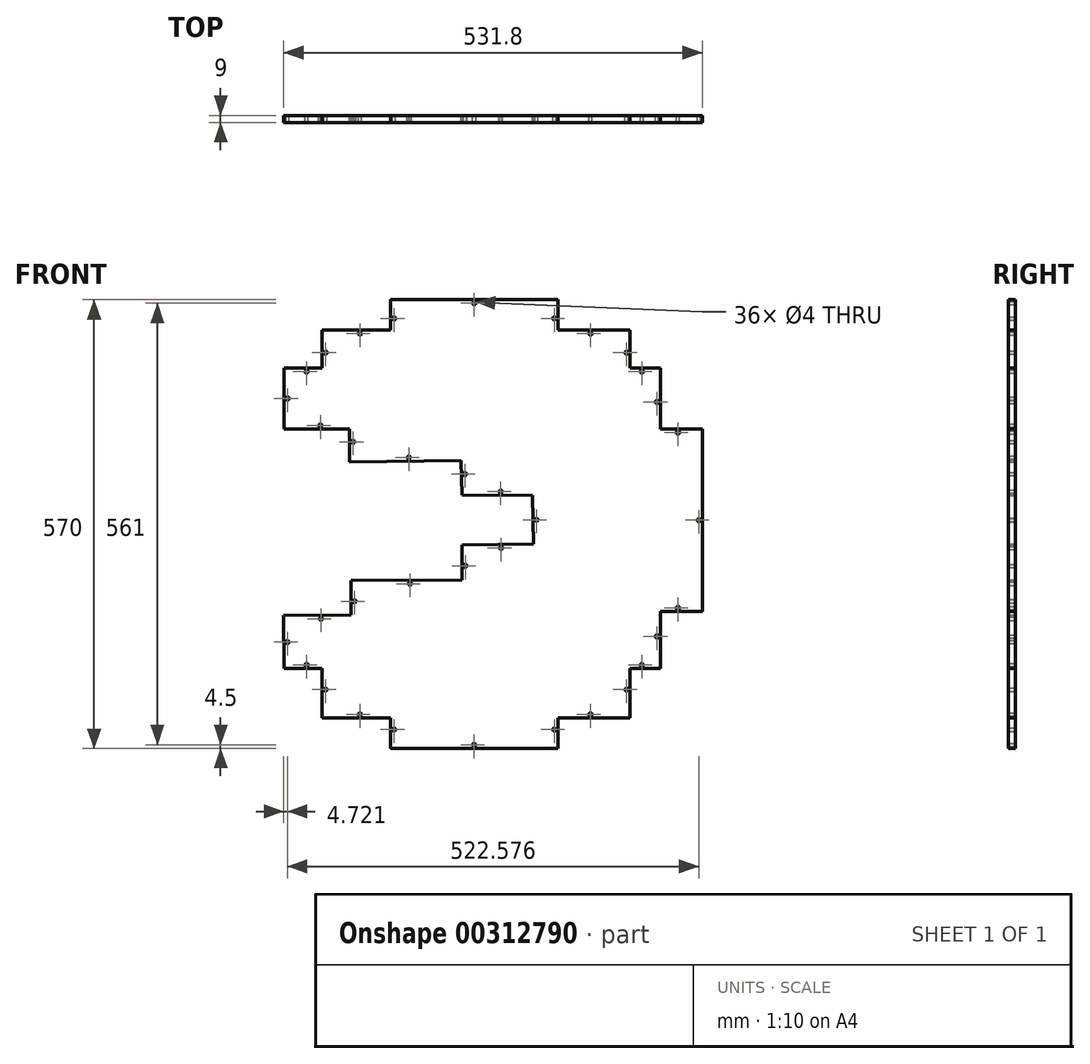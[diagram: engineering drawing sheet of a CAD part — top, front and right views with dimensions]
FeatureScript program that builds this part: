
annotation { "Feature Type Name" : "Feature", "Feature Type Description" : "" }
export const myFeature = defineFeature(function(context is Context, id is Id, definition is map)
    precondition{}
    {
        {
            var Q0;
            Q0=qCreatedBy(makeId("Front.planeOp"),FACE);
            var sketch = newSketch(context, id + "F0", { "sketchPlane" : qUnion([Q0])});
            skLineSegment(sketch, "E0", {"start": v(265.9, 120.76) * mm, "end": v(212.76, 120.76) * mm});
            skLineSegment(sketch, "E1", {"start": v(212.76, 120.76) * mm, "end": v(212.76, 198.05) * mm});
            skLineSegment(sketch, "E2", {"start": v(212.76, 198.05) * mm, "end": v(174.11, 198.05) * mm});
            skLineSegment(sketch, "E3", {"start": v(174.11, 198.05) * mm, "end": v(174.11, 246.35) * mm});
            skLineSegment(sketch, "E4", {"start": v(174.11, 246.35) * mm, "end": v(82.34, 246.35) * mm});
            skLineSegment(sketch, "E5", {"start": v(82.34, 246.35) * mm, "end": v(82.34, 285) * mm});
            skLineSegment(sketch, "E6", {"start": v(82.34, 285) * mm, "end": v(-130.2, 285) * mm});
            skLineSegment(sketch, "E7", {"start": v(-130.2, 285) * mm, "end": v(-130.2, 246.35) * mm});
            skLineSegment(sketch, "E8", {"start": v(-130.2, 246.35) * mm, "end": v(-217.15, 246.35) * mm});
            skLineSegment(sketch, "E9", {"start": v(-217.15, 246.35) * mm, "end": v(-217.15, 198.05) * mm});
            skLineSegment(sketch, "E10", {"start": v(-217.15, 198.05) * mm, "end": v(-265.46, 198.05) * mm});
            skLineSegment(sketch, "E11", {"start": v(-265.46, 198.05) * mm, "end": v(-265.46, 120.76) * mm});
            skLineSegment(sketch, "E12", {"start": v(-265.46, 120.76) * mm, "end": v(-182.22, 120.66) * mm});
            skLineSegment(sketch, "E13", {"start": v(-182.22, 120.66) * mm, "end": v(-182.3, 79) * mm});
            skLineSegment(sketch, "E14", {"start": v(-182.3, 79) * mm, "end": v(-40.62, 80.76) * mm});
            skLineSegment(sketch, "E15", {"start": v(-40.62, 80.76) * mm, "end": v(-39.72, 37.15) * mm});
            skLineSegment(sketch, "E16", {"start": v(-39.72, 37.15) * mm, "end": v(50.2, 36.25) * mm});
            skLineSegment(sketch, "E17", {"start": v(50.2, 36.25) * mm, "end": v(51.12, -25.52) * mm});
            skLineSegment(sketch, "E18", {"start": v(51.12, -25.52) * mm, "end": v(-39.72, -26.43) * mm});
            skLineSegment(sketch, "E19", {"start": v(-39.72, -26.43) * mm, "end": v(-39.72, -70.94) * mm});
            skLineSegment(sketch, "E20", {"start": v(-39.72, -70.94) * mm, "end": v(-180.51, -71.85) * mm});
            skLineSegment(sketch, "E21", {"start": v(-180.51, -71.85) * mm, "end": v(-180.51, -115.45) * mm});
            skLineSegment(sketch, "E22", {"start": v(-180.51, -115.45) * mm, "end": v(-265.9, -116.36) * mm});
            skLineSegment(sketch, "E23", {"start": v(-265.9, -116.36) * mm, "end": v(-265.46, -183.56) * mm});
            skLineSegment(sketch, "E24", {"start": v(-265.46, -183.56) * mm, "end": v(-217.15, -183.56) * mm});
            skLineSegment(sketch, "E25", {"start": v(-217.15, -183.56) * mm, "end": v(-217.15, -246.36) * mm});
            skLineSegment(sketch, "E26", {"start": v(-217.15, -246.36) * mm, "end": v(-130.2, -246.36) * mm});
            skLineSegment(sketch, "E27", {"start": v(-130.2, -246.36) * mm, "end": v(-130.2, -285) * mm});
            skLineSegment(sketch, "E28", {"start": v(-130.2, -285) * mm, "end": v(82.34, -285) * mm});
            skLineSegment(sketch, "E29", {"start": v(82.34, -285) * mm, "end": v(82.34, -246.36) * mm});
            skLineSegment(sketch, "E30", {"start": v(82.34, -246.36) * mm, "end": v(174.11, -246.36) * mm});
            skLineSegment(sketch, "E31", {"start": v(174.11, -246.36) * mm, "end": v(174.11, -183.56) * mm});
            skLineSegment(sketch, "E32", {"start": v(174.11, -183.56) * mm, "end": v(212.76, -183.56) * mm});
            skLineSegment(sketch, "E33", {"start": v(212.76, -183.56) * mm, "end": v(212.76, -111.1) * mm});
            skLineSegment(sketch, "E34", {"start": v(212.76, -111.1) * mm, "end": v(265.9, -111.1) * mm});
            skLineSegment(sketch, "E35", {"start": v(265.9, -111.1) * mm, "end": v(265.9, 120.76) * mm});
            skLineSegment(sketch, "E36.0", {"start": v(261.4, 116.26) * mm, "end": v(208.26, 116.26) * mm, "construction": true});
            skLineSegment(sketch, "E36.1", {"start": v(261.4, -106.6) * mm, "end": v(261.4, 116.26) * mm, "construction": true});
            skLineSegment(sketch, "E36.2", {"start": v(208.26, -106.6) * mm, "end": v(261.4, -106.6) * mm, "construction": true});
            skLineSegment(sketch, "E36.3", {"start": v(208.26, -179.06) * mm, "end": v(208.26, -106.6) * mm, "construction": true});
            skLineSegment(sketch, "E36.4", {"start": v(169.61, -179.06) * mm, "end": v(208.26, -179.06) * mm, "construction": true});
            skLineSegment(sketch, "E36.5", {"start": v(169.61, -241.86) * mm, "end": v(169.61, -179.06) * mm, "construction": true});
            skLineSegment(sketch, "E36.6", {"start": v(77.84, -241.86) * mm, "end": v(169.61, -241.86) * mm, "construction": true});
            skLineSegment(sketch, "E36.7", {"start": v(77.84, -280.5) * mm, "end": v(77.84, -241.86) * mm, "construction": true});
            skLineSegment(sketch, "E36.8", {"start": v(-125.7, -280.5) * mm, "end": v(77.84, -280.5) * mm, "construction": true});
            skLineSegment(sketch, "E36.9", {"start": v(-125.7, -241.86) * mm, "end": v(-125.7, -280.5) * mm, "construction": true});
            skLineSegment(sketch, "E36.10", {"start": v(-212.65, -241.86) * mm, "end": v(-125.7, -241.86) * mm, "construction": true});
            skLineSegment(sketch, "E36.11", {"start": v(208.26, 116.26) * mm, "end": v(208.26, 193.55) * mm, "construction": true});
            skLineSegment(sketch, "E36.12", {"start": v(-212.65, -179.06) * mm, "end": v(-212.65, -241.86) * mm, "construction": true});
            skLineSegment(sketch, "E36.13", {"start": v(-261, -179.06) * mm, "end": v(-212.65, -179.06) * mm, "construction": true});
            skLineSegment(sketch, "E36.14", {"start": v(-260.96, 193.55) * mm, "end": v(-260.96, 125.26) * mm, "construction": true});
            skLineSegment(sketch, "E36.15", {"start": v(-212.65, 193.55) * mm, "end": v(-260.96, 193.55) * mm, "construction": true});
            skLineSegment(sketch, "E36.16", {"start": v(-212.65, 241.85) * mm, "end": v(-212.65, 193.55) * mm, "construction": true});
            skLineSegment(sketch, "E36.17", {"start": v(-125.7, 241.85) * mm, "end": v(-212.65, 241.85) * mm, "construction": true});
            skLineSegment(sketch, "E36.18", {"start": v(-125.7, 280.5) * mm, "end": v(-125.7, 241.85) * mm, "construction": true});
            skLineSegment(sketch, "E36.19", {"start": v(77.84, 280.5) * mm, "end": v(-125.7, 280.5) * mm, "construction": true});
            skLineSegment(sketch, "E36.20", {"start": v(208.26, 193.55) * mm, "end": v(169.61, 193.55) * mm, "construction": true});
            skLineSegment(sketch, "E36.21", {"start": v(169.61, 193.55) * mm, "end": v(169.61, 241.85) * mm, "construction": true});
            skLineSegment(sketch, "E36.22", {"start": v(169.61, 241.85) * mm, "end": v(77.84, 241.85) * mm, "construction": true});
            skLineSegment(sketch, "E36.23", {"start": v(77.84, 241.85) * mm, "end": v(77.84, 280.5) * mm, "construction": true});
            skLineSegment(sketch, "E36.24", {"start": v(-260.96, 125.26) * mm, "end": v(-177.7, 125.15) * mm, "construction": true});
            skLineSegment(sketch, "E36.25", {"start": v(-177.7, 125.15) * mm, "end": v(-177.78, 83.55) * mm, "construction": true});
            skLineSegment(sketch, "E36.26", {"start": v(-177.78, 83.55) * mm, "end": v(-36.22, 85.31) * mm, "construction": true});
            skLineSegment(sketch, "E36.27", {"start": v(-36.22, 85.31) * mm, "end": v(-35.3, 41.6) * mm, "construction": true});
            skLineSegment(sketch, "E36.28", {"start": v(-35.3, 41.6) * mm, "end": v(54.64, 40.7) * mm, "construction": true});
            skLineSegment(sketch, "E36.29", {"start": v(54.64, 40.7) * mm, "end": v(55.69, -29.97) * mm, "construction": true});
            skLineSegment(sketch, "E36.30", {"start": v(55.69, -29.97) * mm, "end": v(-35.22, -30.88) * mm, "construction": true});
            skLineSegment(sketch, "E36.31", {"start": v(-35.22, -30.88) * mm, "end": v(-35.22, -75.4) * mm, "construction": true});
            skLineSegment(sketch, "E36.32", {"start": v(-35.22, -75.4) * mm, "end": v(-176.01, -76.32) * mm, "construction": true});
            skLineSegment(sketch, "E36.33", {"start": v(-176.01, -76.32) * mm, "end": v(-176.01, -119.9) * mm, "construction": true});
            skLineSegment(sketch, "E36.34", {"start": v(-176.01, -119.9) * mm, "end": v(-261.37, -120.82) * mm, "construction": true});
            skLineSegment(sketch, "E36.35", {"start": v(-261.37, -120.82) * mm, "end": v(-261, -179.06) * mm, "construction": true});
            skCircle(sketch, "E37", {"center": v(-23.93, 280.5) * mm, "radius": 2 * mm});
            skCircle(sketch, "E38", {"center": v(-125.7, 261.18) * mm, "radius": 2 * mm});
            skCircle(sketch, "E39", {"center": v(-169.17, 241.85) * mm, "radius": 2 * mm});
            skCircle(sketch, "E40", {"center": v(-212.65, 217.7) * mm, "radius": 2 * mm});
            skCircle(sketch, "E41", {"center": v(-236.8, 193.55) * mm, "radius": 2 * mm});
            skCircle(sketch, "E42", {"center": v(-260.96, 159.4) * mm, "radius": 2 * mm});
            skCircle(sketch, "E43", {"center": v(-219.33, 125.2) * mm, "radius": 2 * mm});
            skCircle(sketch, "E44", {"center": v(-177.75, 104.35) * mm, "radius": 2 * mm});
            skCircle(sketch, "E45", {"center": v(-107, 84.43) * mm, "radius": 2 * mm});
            skCircle(sketch, "E46", {"center": v(-35.76, 63.46) * mm, "radius": 2 * mm});
            skCircle(sketch, "E47", {"center": v(9.67, 41.16) * mm, "radius": 2 * mm});
            skCircle(sketch, "E48", {"center": v(77.84, 261.18) * mm, "radius": 2 * mm});
            skCircle(sketch, "E49", {"center": v(123.73, 241.85) * mm, "radius": 2 * mm});
            skCircle(sketch, "E50", {"center": v(169.61, 217.7) * mm, "radius": 2 * mm});
            skCircle(sketch, "E51", {"center": v(188.94, 193.55) * mm, "radius": 2 * mm});
            skCircle(sketch, "E52", {"center": v(208.26, 154.9) * mm, "radius": 2 * mm});
            skCircle(sketch, "E53", {"center": v(234.83, 116.26) * mm, "radius": 2 * mm});
            skCircle(sketch, "E54", {"center": v(261.4, 4.83) * mm, "radius": 2 * mm});
            skCircle(sketch, "E55", {"center": v(234.83, -106.6) * mm, "radius": 2 * mm});
            skCircle(sketch, "E56", {"center": v(55.17, 5.36) * mm, "radius": 2 * mm});
            skCircle(sketch, "E57", {"center": v(10.24, -30.43) * mm, "radius": 2 * mm});
            skCircle(sketch, "E58", {"center": v(-35.22, -53.15) * mm, "radius": 2 * mm});
            skCircle(sketch, "E59", {"center": v(-105.61, -75.86) * mm, "radius": 2 * mm});
            skCircle(sketch, "E60", {"center": v(-176.01, -98.1) * mm, "radius": 2 * mm});
            skCircle(sketch, "E61", {"center": v(-218.69, -120.36) * mm, "radius": 2 * mm});
            skCircle(sketch, "E62", {"center": v(-261.18, -149.94) * mm, "radius": 2 * mm});
            skCircle(sketch, "E63", {"center": v(-236.82, -179.06) * mm, "radius": 2 * mm});
            skCircle(sketch, "E64", {"center": v(-212.65, -210.46) * mm, "radius": 2 * mm});
            skCircle(sketch, "E65", {"center": v(-169.17, -241.86) * mm, "radius": 2 * mm});
            skCircle(sketch, "E66", {"center": v(-125.7, -261.18) * mm, "radius": 2 * mm});
            skCircle(sketch, "E67", {"center": v(-23.93, -280.5) * mm, "radius": 2 * mm});
            skCircle(sketch, "E68", {"center": v(77.84, -261.18) * mm, "radius": 2 * mm});
            skCircle(sketch, "E69", {"center": v(123.73, -241.86) * mm, "radius": 2 * mm});
            skCircle(sketch, "E70", {"center": v(169.61, -210.46) * mm, "radius": 2 * mm});
            skCircle(sketch, "E71", {"center": v(188.94, -179.06) * mm, "radius": 2 * mm});
            skCircle(sketch, "E72", {"center": v(208.26, -142.83) * mm, "radius": 2 * mm});
            skSolve(sketch);
        }
        {
            var Q0;
            Q0 = qSketchRegion(id + "F0", true);
            extrude(context, id + "F1", {"entities" : qUnion([Q0]), "depth" : 9 * mm});
        }
    });
